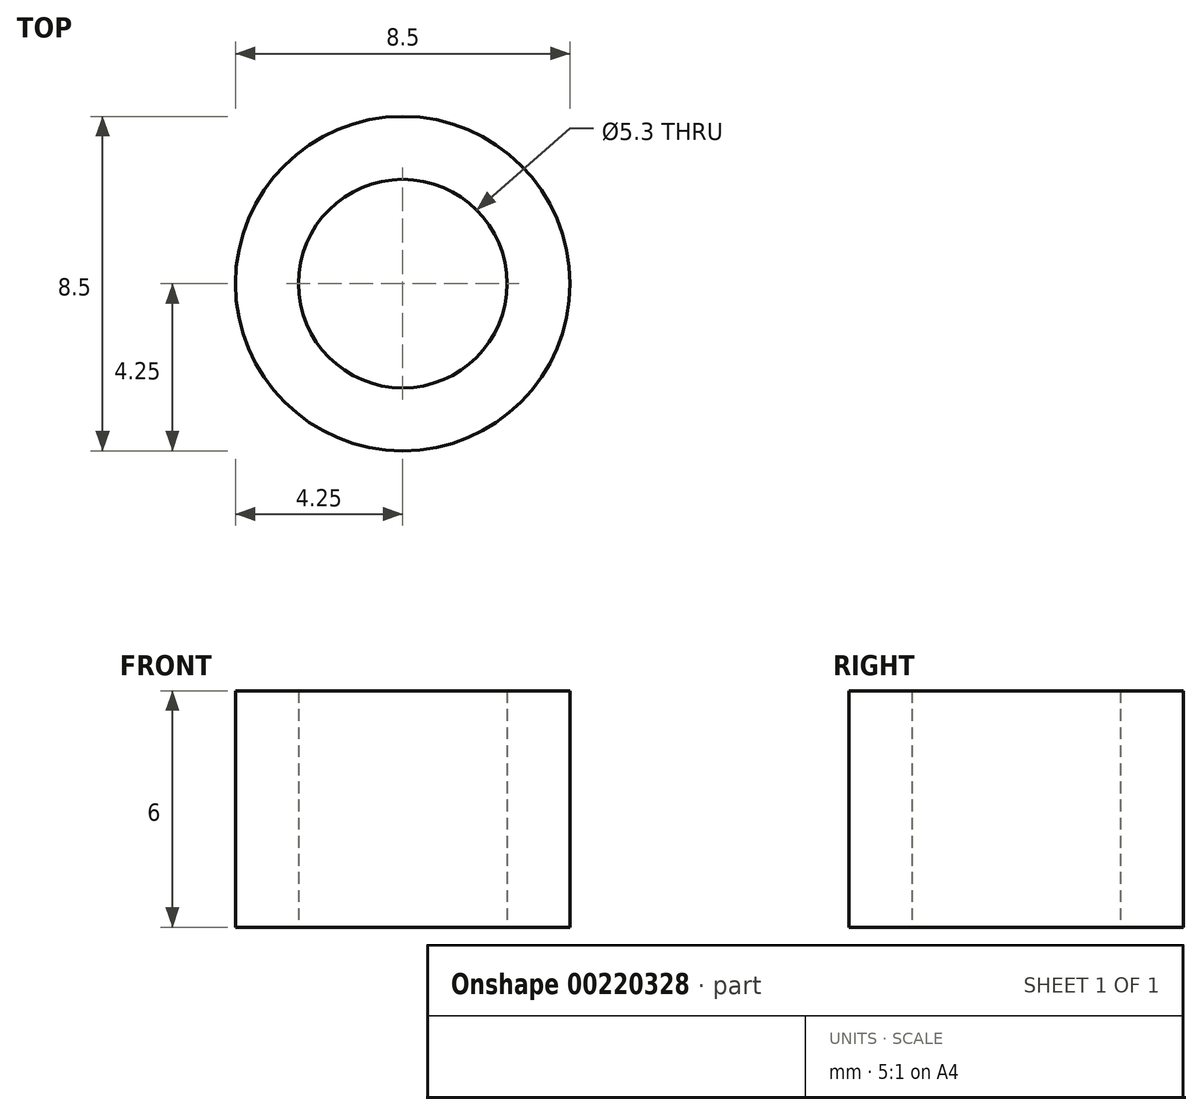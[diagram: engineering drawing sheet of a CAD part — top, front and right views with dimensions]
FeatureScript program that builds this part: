
annotation { "Feature Type Name" : "Feature", "Feature Type Description" : "" }
export const myFeature = defineFeature(function(context is Context, id is Id, definition is map)
    precondition{}
    {
        {
            var Q0;
            Q0=qCreatedBy(makeId("Top.planeOp"),FACE);
            var sketch = newSketch(context, id + "F0", { "sketchPlane" : qUnion([Q0])});
            skCircle(sketch, "E0", {"center": v(0, 0) * mm, "radius": 2.65 * mm});
            skCircle(sketch, "E1", {"center": v(0, 0) * mm, "radius": 4.25 * mm});
            skSolve(sketch);
        }
        {
            var Q0;
            Q0=qSketchRegion(id+"F0",true);
            extrude(context, id + "F1", {"entities" : qUnion([Q0]), "depth" : 6 * mm});
        }
    });
